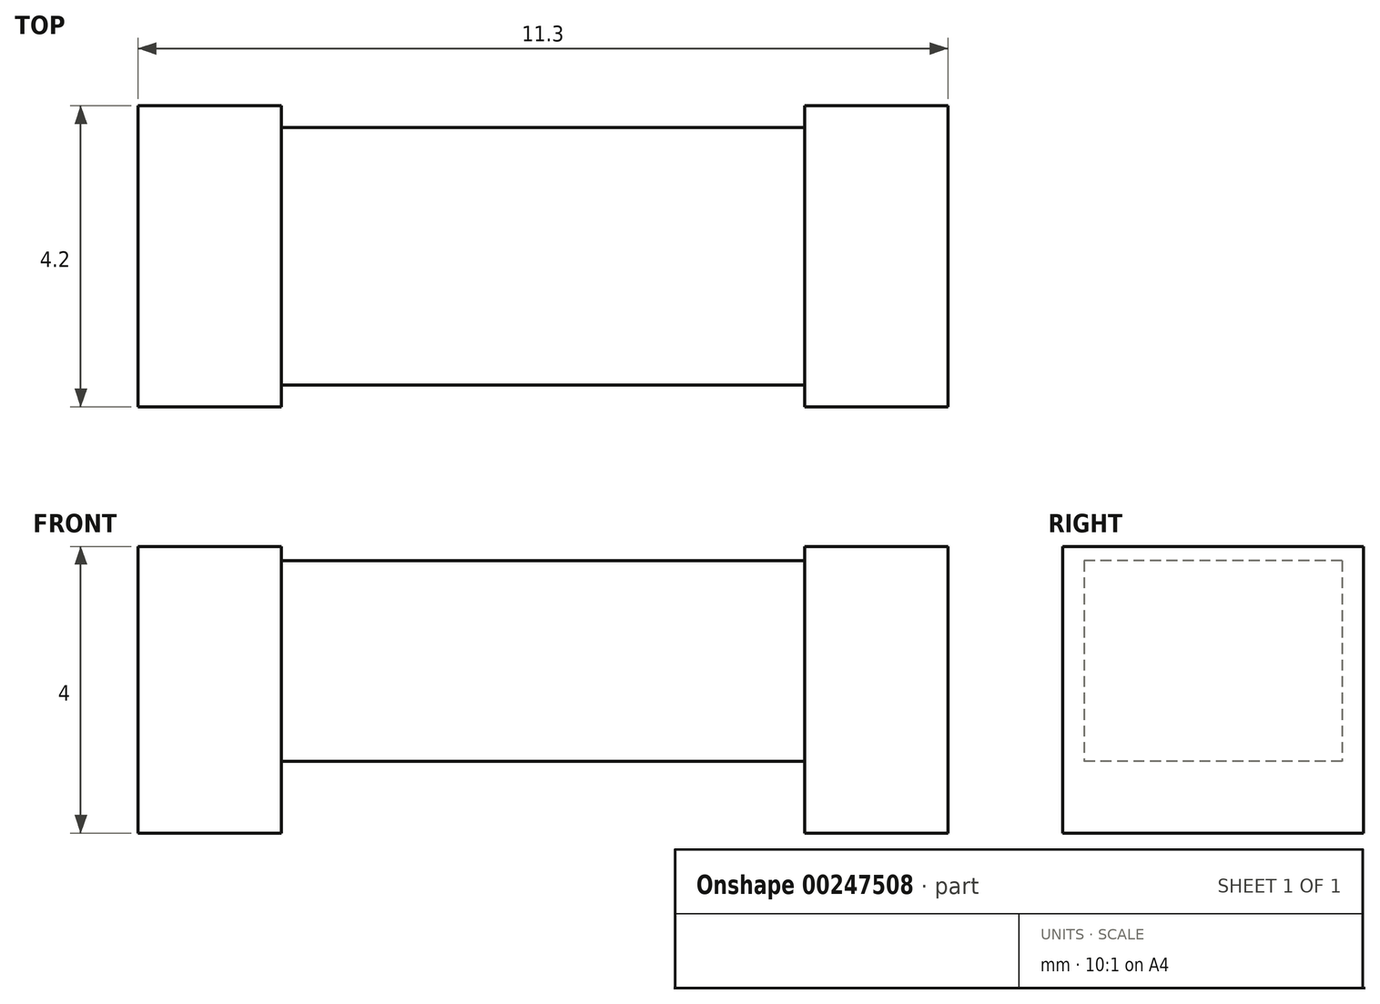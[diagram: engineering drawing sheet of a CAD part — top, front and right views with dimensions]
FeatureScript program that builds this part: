
annotation { "Feature Type Name" : "Feature", "Feature Type Description" : "" }
export const myFeature = defineFeature(function(context is Context, id is Id, definition is map)
    precondition{}
    {
        {
            var Q0;
            Q0=qCreatedBy(makeId("Top.planeOp"),FACE);
            var sketch = newSketch(context, id + "F0", { "sketchPlane" : qUnion([Q0])});
            skLineSegment(sketch, "E0", {"start": v(-10.8, 0) * mm, "end": v(10.52, 0) * mm, "construction": true});
            skLineSegment(sketch, "E1", {"start": v(0, -4.6) * mm, "end": v(0, 5.7) * mm, "construction": true});
            skLineSegment(sketch, "E2.bottom", {"start": v(-3.65, -2.1) * mm, "end": v(-5.65, -2.1) * mm});
            skLineSegment(sketch, "E2.top", {"start": v(-3.65, 2.1) * mm, "end": v(-5.65, 2.1) * mm});
            skLineSegment(sketch, "E2.left", {"start": v(-3.65, -2.1) * mm, "end": v(-3.65, 2.1) * mm});
            skLineSegment(sketch, "E2.right", {"start": v(-5.65, -2.1) * mm, "end": v(-5.65, 2.1) * mm});
            skPoint(sketch, "E2.middle", {"position": v(-4.65, 0) * mm});
            skPoint(sketch, "E3.MirrorP", {"position": v(4.65, 0) * mm});
            skLineSegment(sketch, "E4.MirrorCS", {"start": v(5.65, -2.1) * mm, "end": v(5.65, 2.1) * mm});
            skLineSegment(sketch, "E5.MirrorCS", {"start": v(3.65, -2.1) * mm, "end": v(3.65, 2.1) * mm});
            skLineSegment(sketch, "E6.MirrorCS", {"start": v(3.65, 2.1) * mm, "end": v(5.65, 2.1) * mm});
            skLineSegment(sketch, "E7.MirrorCS", {"start": v(10.8, 0) * mm, "end": v(-10.52, 0) * mm, "construction": true});
            skLineSegment(sketch, "E8.MirrorCS", {"start": v(3.65, -2.1) * mm, "end": v(5.65, -2.1) * mm});
            skSolve(sketch);
        }
        {
            var Q0;
            Q0 = qSketchRegion(id + "F0", true);
            extrude(context, id + "F1", {"entities" : qUnion([Q0]), "depth" : 4 * mm});
        }
        {
            var Q0;
            Q0=makeQuery(id+"F1.opExtrude","SWEPT_FACE",FACE,{"disambiguationData":[OSD([sQuery(id+"F0.wireOp",EDGE,"E2.left")])]});
            var sketch = newSketch(context, id + "F2", { "sketchPlane" : qUnion([Q0])});
            skLineSegment(sketch, "E9", {"start": v(0, 4) * mm, "end": v(0, 0) * mm, "construction": true});
            skLineSegment(sketch, "E10.bottom", {"start": v(-1.8, 1) * mm, "end": v(1.8, 1) * mm});
            skLineSegment(sketch, "E10.top", {"start": v(-1.8, 3.8) * mm, "end": v(1.8, 3.8) * mm});
            skLineSegment(sketch, "E10.left", {"start": v(-1.8, 1) * mm, "end": v(-1.8, 3.8) * mm});
            skLineSegment(sketch, "E10.right", {"start": v(1.8, 1) * mm, "end": v(1.8, 3.8) * mm});
            skPoint(sketch, "E10.middle", {"position": v(0, 2.4) * mm});
            skSolve(sketch);
        }
        {
            var Q0;
            Q0 = qSketchRegion(id + "F2", true);
            extrude(context, id + "F3", {"entities" : qUnion([Q0]), "endBound" : BoundingType.UP_TO_NEXT, "depth" : 25 * mm});
        }
    });
